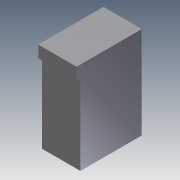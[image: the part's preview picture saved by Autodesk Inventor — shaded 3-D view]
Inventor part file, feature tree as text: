
AUTODESK INVENTOR PART (.ipt)
format: ipt  version: 2011 (Build 150239000, 239)  size: 83,456 bytes
history: native  units: in
note: dims shown in document units (in); Inventor stores cm internally (conversion verified against a paired STEP export)
features: extrude x3, sketch x3
ambient origin geometry x8: Origin, YZ Plane, XZ Plane, XY Plane, X Axis, Y Axis, Z Axis, Center Point
bodies: Solid1 (feature_tree)
feature tree (6):
  extrude  "Extrusion1"  Depth=6.0in
  extrude  "Extrusion2"  Depth=0.25in TaperAngle=0.0deg
  extrude  "Extrusion3"  [1 undecoded]
  sketch  "Sketch1"  dims[d0=2.5in d1=6.0in]
  sketch  "Sketch2"  dims[d2=4.5in d3=0.0in d4=0.25in d5=0.0in]
  sketch  "Sketch3"  dims[d6=0.25in d7=0.0in]
note: 1 required parameter value undecoded (feature->parameter linkage not recoverable at this tier; creation-order binding heuristic only, values carry confidence <= 0.55)
